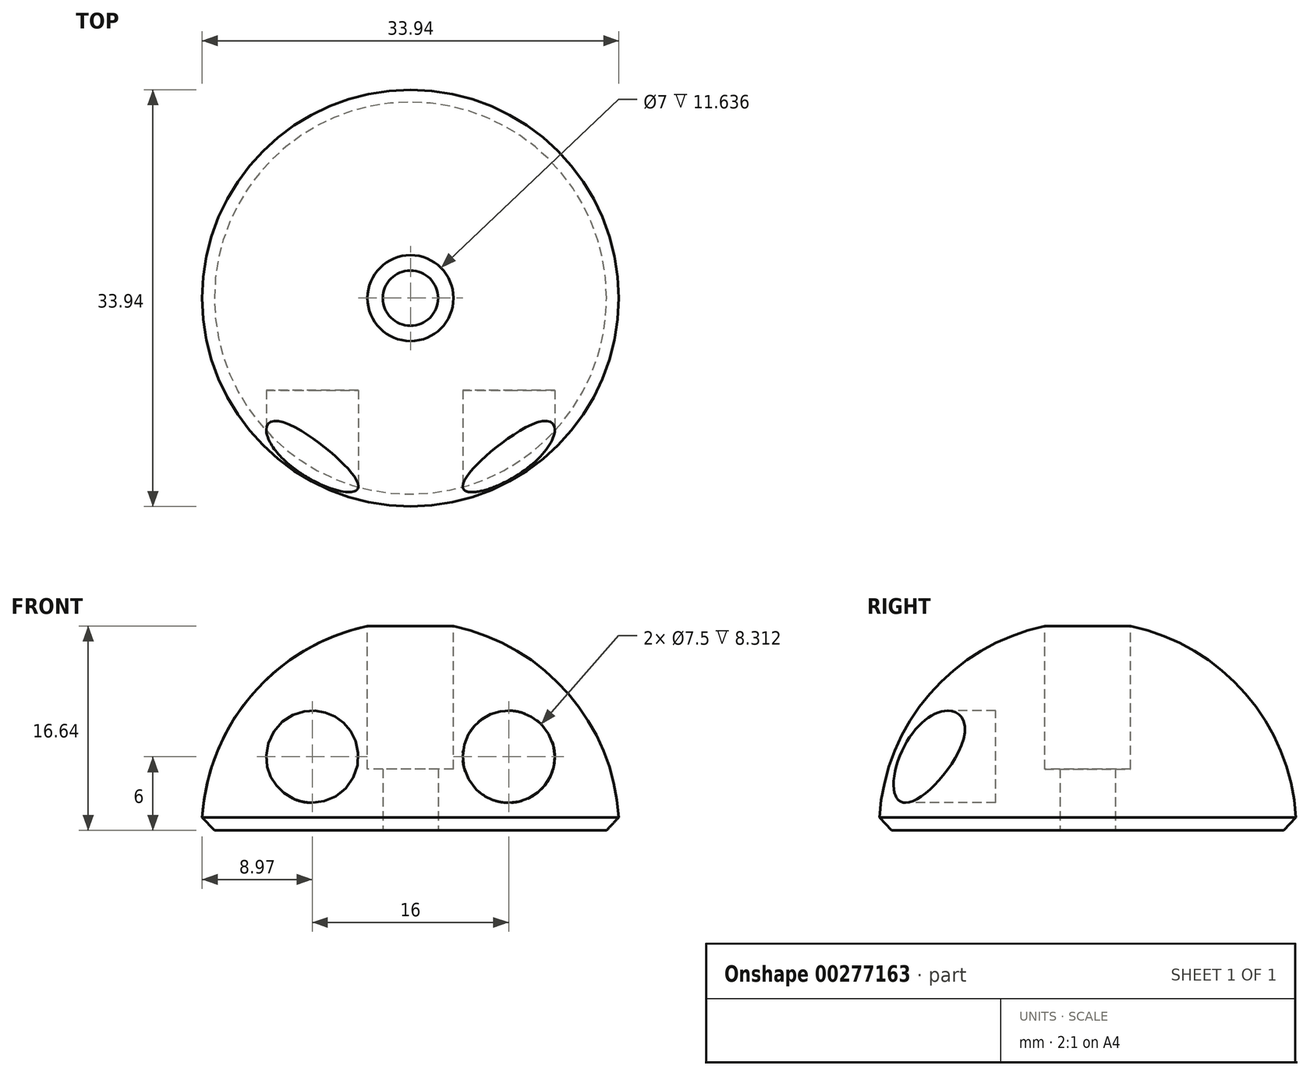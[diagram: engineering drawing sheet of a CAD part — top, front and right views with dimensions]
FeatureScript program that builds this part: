
annotation { "Feature Type Name" : "Feature", "Feature Type Description" : "" }
export const myFeature = defineFeature(function(context is Context, id is Id, definition is map)
    precondition{}
    {
        {
            var Q0;
            Q0=qCreatedBy(makeId("Front.planeOp"),FACE);
            var sketch = newSketch(context, id + "F0", { "sketchPlane" : qUnion([Q0])});
            skLineSegment(sketch, "E0", {"start": v(17, 0) * mm, "end": v(0, 0) * mm});
            skArc(sketch, "E1", {"start": v(17, 0) * mm, "mid": v(12.02, 12.02) * mm, "end": v(0, 17) * mm});
            skLineSegment(sketch, "E2.trimOffspring", {"start": v(0, 0) * mm, "end": v(0, 17) * mm});
            skSolve(sketch);
        }
        {
            var Q0;
            Q0=qSketchRegion(id+"F0",true);
            var Q1;
            Q1=sQuery(id+"F0.wireOp",EDGE,"E2.trimOffspring");
            revolve(context, id + "F1", {"entities" : qUnion([Q0]), "axis" : qUnion([Q1]), "revolveType" : RevolveType.FULL});
        }
        {
            var Q0;
            Q0=qCreatedBy(makeId("Front.planeOp"),FACE);
            cPlane(context, id + "F2", {"entities" : qUnion([Q0]), "cplaneType" : CPlaneType.OFFSET, "offset" : 15 * mm, "width" : 150 * mm, "height" : 150 * mm});
        }
        {
            var Q0;
            Q0=qCreatedBy(id+"F2.planeOp",FACE);
            var sketch = newSketch(context, id + "F3", { "sketchPlane" : qUnion([Q0])});
            skCircle(sketch, "E3", {"center": v(-8, 6) * mm, "radius": 3.75 * mm});
            skCircle(sketch, "E4.MirrorC", {"center": v(8, 6) * mm, "radius": 3.75 * mm});
            skSolve(sketch);
        }
        {
            var Q0;
            Q0=qSketchRegion(id+"F3",true);
            extrude(context, id + "F4", {"entities" : qUnion([Q0]), "operationType" : NewBodyOperationType.REMOVE, "endBound" : BoundingType.SYMMETRIC, "oppositeDirection" : true, "depth" : 15 * mm});
        }
        {
            var Q0;
            Q0=makeQuery(id+"F1.opRevolve","SWEPT_EDGE",EDGE,{"disambiguationData":[OSD([sQuery(id+"F0.wireOp",EDGE,"E0"),sQuery(id+"F0.wireOp",EDGE,"E1")])]});
            chamfer(context, id + "F5", {"entities" : qUnion([Q0]), "width" : 1 * mm, "tangentPropagation" : true});
        }
        {
            var Q0;
            Q0=qCreatedBy(makeId("Top.planeOp"),FACE);
            var sketch = newSketch(context, id + "F6", { "sketchPlane" : qUnion([Q0])});
            skCircle(sketch, "E5", {"center": v(0, 0) * mm, "radius": 2.25 * mm});
            skSolve(sketch);
        }
        {
            var Q0;
            Q0=qSketchRegion(id+"F6",true);
            extrude(context, id + "F7", {"entities" : qUnion([Q0]), "operationType" : NewBodyOperationType.REMOVE, "endBound" : BoundingType.THROUGH_ALL, "depth" : 25 * mm});
        }
        {
            var Q0;
            Q0=qCreatedBy(makeId("Top.planeOp"),FACE);
            cPlane(context, id + "F8", {"entities" : qUnion([Q0]), "cplaneType" : CPlaneType.OFFSET, "offset" : 30 * mm, "width" : 150 * mm, "height" : 150 * mm});
        }
        {
            var Q0;
            Q0=qCreatedBy(id+"F8.planeOp",FACE);
            var sketch = newSketch(context, id + "F9", { "sketchPlane" : qUnion([Q0])});
            skCircle(sketch, "E6", {"center": v(0, 0) * mm, "radius": 3.5 * mm});
            skSolve(sketch);
        }
        {
            var Q0;
            Q0=qSketchRegion(id+"F9",true);
            extrude(context, id + "F10", {"entities" : qUnion([Q0]), "operationType" : NewBodyOperationType.REMOVE, "oppositeDirection" : true, "depth" : 25 * mm});
        }
    });
